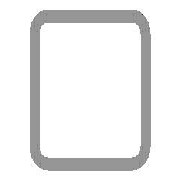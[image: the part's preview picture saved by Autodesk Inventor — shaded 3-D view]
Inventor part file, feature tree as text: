
AUTODESK INVENTOR PART (.ipt)
format: ipt  version: 2024.3 (Build 283343000, 343)  size: 142,848 bytes
history: native  units: mm (DEFAULTED — no unit token found)
features: other x4, plane x2, split x1, sketch x1
ambient origin geometry x8: Origin, YZ Plane, XZ Plane, XY Plane, X Axis, Y Axis, Z Axis, Center Point
bodies: Solid1 (feature_tree), Body (feature_tree)
feature tree (8):
  parser-record x1  (decoder bookkeeping rows leaked as tree rows — omitted from the tree; the rows remain in map.json)
  other  "Driven Length"
  other  "Start Plane"
  other  "End Plane"
  plane  "Work Plane4"
  split  "Split1"
  sketch  "Sketch3"  dims[d3=254.989146mm d4=0.0mm d7=6.0mm d9=100.0mm d11=100.0mm d12=3.0mm d13=-0.0mm d14=254.989146mm d15=50.0mm d16=50.0mm d17=90.0deg d18=254.989146mm]
  plane  "Work Plane3"
